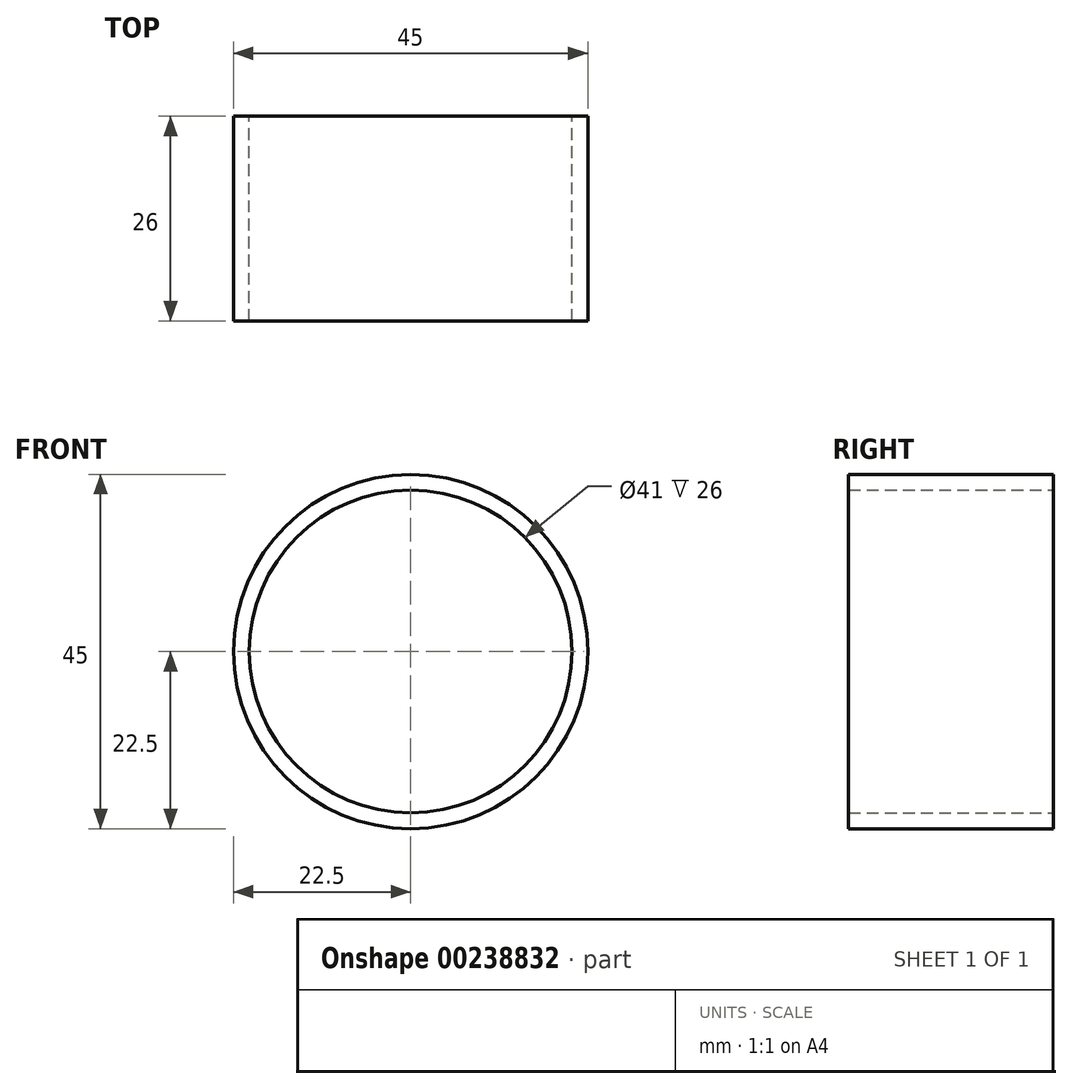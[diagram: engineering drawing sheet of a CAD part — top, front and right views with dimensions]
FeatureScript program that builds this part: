
annotation { "Feature Type Name" : "Feature", "Feature Type Description" : "" }
export const myFeature = defineFeature(function(context is Context, id is Id, definition is map)
    precondition{}
    {
        {
            var Q0;
            Q0=qCreatedBy(makeId("Front.planeOp"),FACE);
            var sketch = newSketch(context, id + "F0", { "sketchPlane" : qUnion([Q0])});
            skCircle(sketch, "E0", {"center": v(0, 0) * mm, "radius": 22.5 * mm});
            skCircle(sketch, "E1", {"center": v(0, 0) * mm, "radius": 20.5 * mm});
            skSolve(sketch);
        }
        {
            var Q0;
            Q0=makeQuery(id+"F0.imprint","IMPRINT",FACE,{"disambiguationData":[TD([[makeQuery(id+"F0.imprint","IMPRINT",EDGE,{"derivedFrom":sQuery(id+"F0.wireOp",EDGE,"E0")}),1.0]])]});
            extrude(context, id + "F1", {"entities" : qUnion([Q0]), "depth" : 26 * mm});
        }
    });
